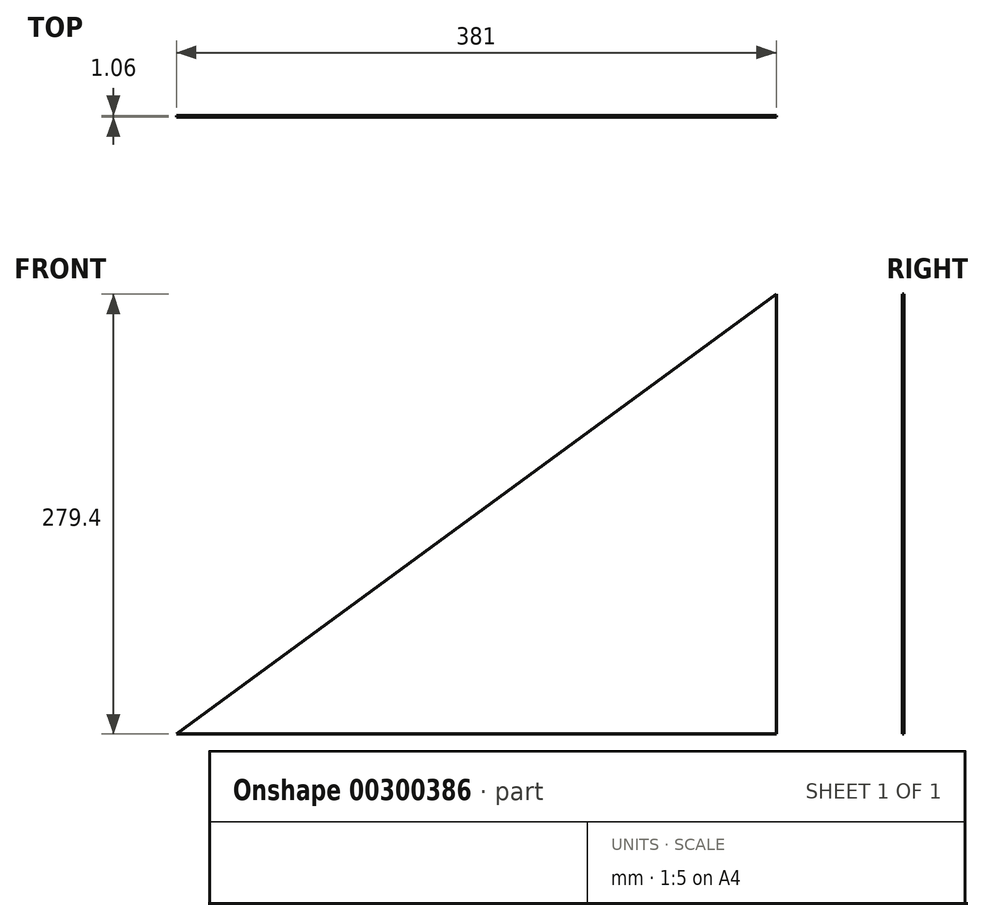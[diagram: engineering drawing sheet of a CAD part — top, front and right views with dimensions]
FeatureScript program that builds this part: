
annotation { "Feature Type Name" : "Feature", "Feature Type Description" : "" }
export const myFeature = defineFeature(function(context is Context, id is Id, definition is map)
    precondition{}
    {
        {
            var Q0;
            Q0=qCreatedBy(makeId("Front.planeOp"),FACE);
            var sketch = newSketch(context, id + "F0", { "sketchPlane" : qUnion([Q0])});
            skLineSegment(sketch, "E0", {"start": v(148.43, 42.64) * mm, "end": v(148.43, -236.76) * mm});
            skLineSegment(sketch, "E1", {"start": v(148.43, -236.76) * mm, "end": v(-232.57, -236.76) * mm});
            skLineSegment(sketch, "E2", {"start": v(-232.57, -236.76) * mm, "end": v(148.43, 42.64) * mm});
            skSolve(sketch);
        }
        {
            var Q0;
            Q0=makeQuery(id+"F0.imprint","IMPRINT",FACE,{"disambiguationData":[TD([[makeQuery(id+"F0.imprint","IMPRINT",EDGE,{"derivedFrom":sQuery(id+"F0.wireOp",EDGE,"E0")}),-1.0]])]});
            extrude(context, id + "F1", {"entities" : qUnion([Q0]), "depth" : 1.06 * mm});
        }
    });
